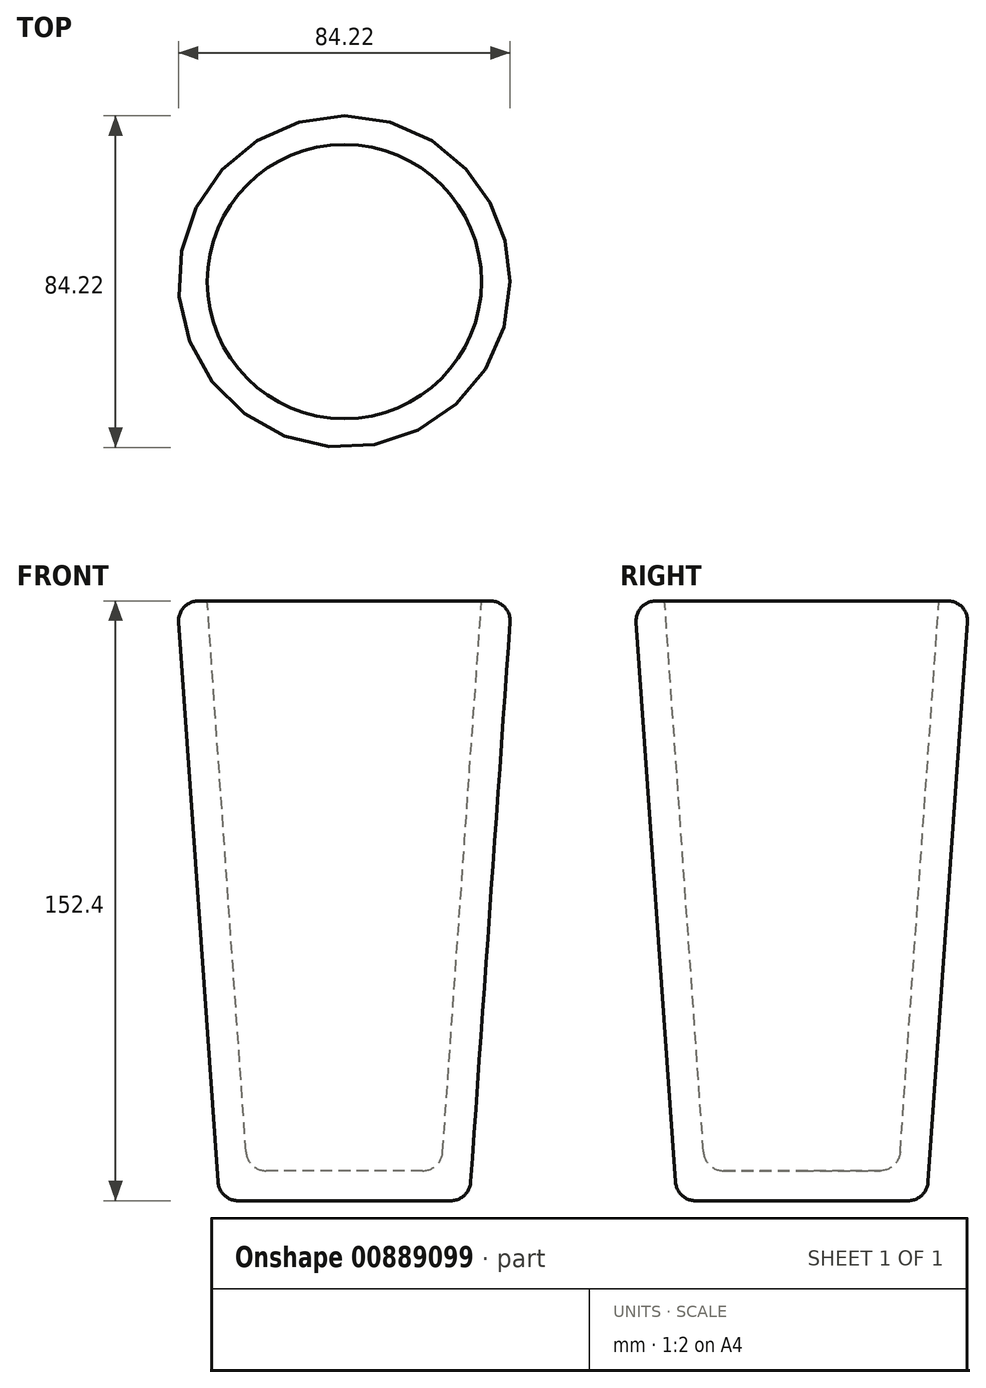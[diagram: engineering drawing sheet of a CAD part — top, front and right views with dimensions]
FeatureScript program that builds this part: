
annotation { "Feature Type Name" : "Feature", "Feature Type Description" : "" }
export const myFeature = defineFeature(function(context is Context, id is Id, definition is map)
    precondition{}
    {
        {
            var Q0;
            Q0=qCreatedBy(makeId("Top.planeOp"),FACE);
            var sketch = newSketch(context, id + "F0", { "sketchPlane" : qUnion([Q0])});
            skCircle(sketch, "E0", {"center": v(0, 0) * mm, "radius": 31.75 * mm});
            skSolve(sketch);
        }
        {
            var Q0;
            Q0=qCreatedBy(makeId("Top.planeOp"),FACE);
            cPlane(context, id + "F1", {"entities" : qUnion([Q0]), "cplaneType" : CPlaneType.OFFSET, "offset" : 152.4 * mm, "width" : 152.4 * mm, "height" : 152.4 * mm});
        }
        {
            var Q0;
            Q0=qCreatedBy(id+"F1.planeOp",FACE);
            var sketch = newSketch(context, id + "F2", { "sketchPlane" : qUnion([Q0])});
            skCircle(sketch, "E1", {"center": v(0, 0) * mm, "radius": 42.48 * mm});
            skSolve(sketch);
        }
        {
            var Q0;
            Q0=makeQuery(id+"F0.imprint","IMPRINT",FACE,{"disambiguationData":[TD([[makeQuery(id+"F0.imprint","IMPRINT",EDGE,{"derivedFrom":sQuery(id+"F0.wireOp",EDGE,"E0")}),1.0]])]});
            var Q1;
            Q1=makeQuery(id+"F2.imprint","IMPRINT",FACE,{"disambiguationData":[TD([[makeQuery(id+"F2.imprint","IMPRINT",EDGE,{"derivedFrom":sQuery(id+"F2.wireOp",EDGE,"E1")}),1.0]])]});
            loft(context, id + "F3", {"sheetProfilesArray" : [{ "sheetProfileEntities" : qUnion([Q0]) }, { "sheetProfileEntities" : qUnion([Q1]) }]});
        }
        {
            var Q0;
            Q0=makeQuery(id+"F3.opLoft","CAP_FACE",FACE,{"disambiguationData":[OSD([makeQuery(id+"F2.imprint","IMPRINT",FACE,{"disambiguationData":[TD([[makeQuery(id+"F2.imprint","IMPRINT",EDGE,{"derivedFrom":sQuery(id+"F2.wireOp",EDGE,"E1")}),1.0]])]})])],"isStart":true});
            shell(context, id + "F4", {"entities" : qUnion([Q0]), "thickness" : 7.62 * mm});
        }
        {
            var Q0;
            Q0=makeQuery(id+"F3.opLoft","MID_CAP_EDGE",EDGE,{"disambiguationData":[OSD([sQuery(id+"F2.wireOp",EDGE,"E1")])],"capPos":1.0});
            fillet(context, id + "F5", {"entities" : qUnion([Q0]), "radius" : 5.08 * mm, "tangentPropagation" : true, "allowEdgeOverflow" : false});
        }
        {
            var Q0;
            Q0=makeQuery(id+"F3.opLoft","CAP_FACE",FACE,{"disambiguationData":[OSD([makeQuery(id+"F0.imprint","IMPRINT",FACE,{"disambiguationData":[TD([[makeQuery(id+"F0.imprint","IMPRINT",EDGE,{"derivedFrom":sQuery(id+"F0.wireOp",EDGE,"E0")}),1.0]])]})])],"isStart":true});
            fillet(context, id + "F6", {"entities" : qUnion([Q0]), "radius" : 5.08 * mm, "tangentPropagation" : true, "allowEdgeOverflow" : false});
        }
        {
            var Q0;
            Q0=makeQuery(id+"F4.opShell","OFFSET_EDGE",EDGE,{"disambiguationData":[OSD([sQuery(id+"F0.wireOp",EDGE,"E0")])]});
            fillet(context, id + "F7", {"entities" : qUnion([Q0]), "radius" : 5.08 * mm, "tangentPropagation" : true, "allowEdgeOverflow" : false});
        }
    });
